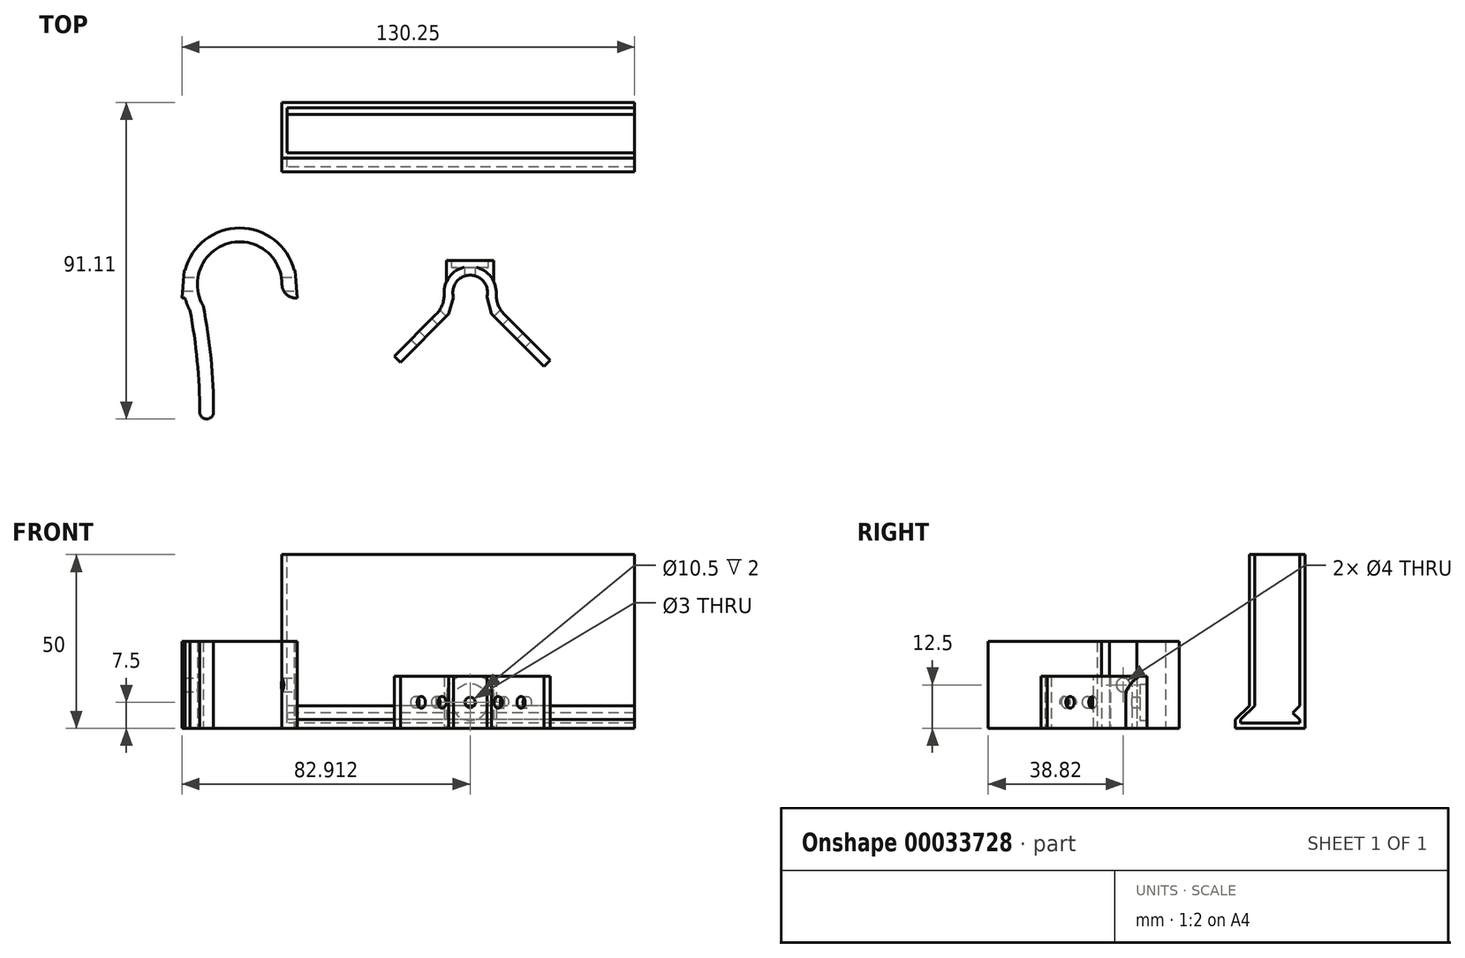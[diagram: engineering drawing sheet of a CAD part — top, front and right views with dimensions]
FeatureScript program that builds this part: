
annotation { "Feature Type Name" : "Feature", "Feature Type Description" : "" }
export const myFeature = defineFeature(function(context is Context, id is Id, definition is map)
    precondition{}
    {
        {
            var Q0;
            Q0=qCreatedBy(makeId("Top.planeOp"),FACE);
            var sketch = newSketch(context, id + "F0", { "sketchPlane" : qUnion([Q0])});
            skLineSegment(sketch, "E0", {"start": v(-6.16, 14.57) * mm, "end": v(-6.16, -16.07) * mm, "construction": true});
            skLineSegment(sketch, "E1.0", {"start": v(-21.16, 14.57) * mm, "end": v(-21.16, -16.07) * mm, "construction": true});
            skLineSegment(sketch, "E2.0", {"start": v(-24.16, 14.57) * mm, "end": v(-24.16, -16.07) * mm, "construction": true});
            skLineSegment(sketch, "E3.0", {"start": v(-3.16, 14.57) * mm, "end": v(-3.16, -16.07) * mm, "construction": true});
            skArc(sketch, "E4", {"start": v(-3.16, 14.57) * mm, "mid": v(-13.66, 32.92) * mm, "end": v(-24.16, 14.57) * mm});
            skArc(sketch, "E5", {"start": v(-21.16, -16.07) * mm, "mid": v(-21.91, -0.67) * mm, "end": v(-24.16, 14.57) * mm});
            skLineSegment(sketch, "E6", {"start": v(-13.66, 20.74) * mm, "end": v(-13.66, -32.7) * mm, "construction": true});
            skArc(sketch, "E7.0", {"start": v(-25.16, -16.07) * mm, "mid": v(-25.86, -1.38) * mm, "end": v(-27.97, 13.18) * mm});
            skArc(sketch, "E7.1", {"start": v(0.29, 12.55) * mm, "mid": v(-13.3, 36.92) * mm, "end": v(-27.97, 13.18) * mm});
            skArc(sketch, "E8", {"start": v(-25.16, -16.07) * mm, "mid": v(-23.16, -18.07) * mm, "end": v(-21.16, -16.07) * mm});
            skArc(sketch, "E9.MirrorCS", {"start": v(-6.16, -16.07) * mm, "mid": v(-5.4, -0.67) * mm, "end": v(-3.16, 14.57) * mm});
            skArc(sketch, "E10.MirrorCS", {"start": v(-2.16, -16.07) * mm, "mid": v(-1.46, -1.38) * mm, "end": v(0.64, 13.18) * mm});
            skArc(sketch, "E11.MirrorCS", {"start": v(-2.16, -16.07) * mm, "mid": v(-4.16, -18.07) * mm, "end": v(-6.16, -16.07) * mm});
            skCircle(sketch, "E12", {"center": v(-29.84, 20.74) * mm, "radius": 4 * mm});
            skLineSegment(sketch, "E13", {"start": v(-28.93, 31.84) * mm, "end": v(-30.86, 9.83) * mm});
            skLineSegment(sketch, "E14.MirrorCS", {"start": v(1.6, 31.84) * mm, "end": v(3.53, 9.83) * mm});
            skCircle(sketch, "E15.MirrorC", {"center": v(2.52, 20.74) * mm, "radius": 4 * mm});
            skSolve(sketch);
        }
        {
            var Q0;
            {var subQ6=sQuery(id+"F0.wireOp",EDGE,"E5");Q0=makeQuery(id+"F0.imprint","IMPRINT",FACE,{"disambiguationData":[TD([[makeQuery(id+"F0.imprint","IMPRINT",EDGE,{"derivedFrom":subQ6}),1.0]])]});}
            var Q1;
            {var subQ1=sQuery(id+"F0.wireOp",EDGE,"E9.MirrorCS");Q1=makeQuery(id+"F0.imprint","IMPRINT",FACE,{"disambiguationData":[TD([[makeQuery(id+"F0.imprint","IMPRINT",EDGE,{"derivedFrom":subQ1}),-1.0]])]});}
            var Q2;
            {var subQ0=sQuery(id+"F0.wireOp",EDGE,"E15.MirrorC");var subQ1=sQuery(id+"F0.wireOp",EDGE,"E4");var subQ2=makeQuery(id+"F0.imprint","INTERSECT",VERTEX,{"derivedFrom":[subQ1,subQ0]});Q2=makeQuery(id+"F0.imprint","IMPRINT",FACE,{"disambiguationData":[TD([[makeQuery(id+"F0.imprint","IMPRINT",EDGE,{"disambiguationData":[TD([[subQ2,-1.0]])],"derivedFrom":subQ1}),-1.0]])]});}
            var Q3;
            {var subQ0=sQuery(id+"F0.wireOp",EDGE,"E14.MirrorCS");var subQ1=sQuery(id+"F0.wireOp",EDGE,"E7.1");var subQ2=makeQuery(id+"F0.imprint","INTERSECT",VERTEX,{"derivedFrom":[subQ1,subQ0]});Q3=makeQuery(id+"F0.imprint","IMPRINT",FACE,{"disambiguationData":[TD([[makeQuery(id+"F0.imprint","IMPRINT",EDGE,{"disambiguationData":[TD([[subQ2,-1.0]])],"derivedFrom":subQ1}),-1.0]])]});}
            var Q4;
            {var subQ0=sQuery(id+"F0.wireOp",EDGE,"E13");var subQ1=sQuery(id+"F0.wireOp",EDGE,"E7.1");var subQ2=makeQuery(id+"F0.imprint","INTERSECT",VERTEX,{"derivedFrom":[subQ1,subQ0]});Q4=makeQuery(id+"F0.imprint","IMPRINT",FACE,{"disambiguationData":[TD([[makeQuery(id+"F0.imprint","IMPRINT",EDGE,{"disambiguationData":[TD([[subQ2,1.0]])],"derivedFrom":subQ1}),-1.0]])]});}
            var Q5;
            {var subQ0=sQuery(id+"F0.wireOp",EDGE,"E13");var subQ1=sQuery(id+"F0.wireOp",EDGE,"E7.1");var subQ2=makeQuery(id+"F0.imprint","INTERSECT",VERTEX,{"derivedFrom":[subQ1,subQ0]});Q5=makeQuery(id+"F0.imprint","IMPRINT",FACE,{"disambiguationData":[TD([[makeQuery(id+"F0.imprint","IMPRINT",EDGE,{"disambiguationData":[TD([[subQ2,-1.0]])],"derivedFrom":subQ1}),-1.0]])]});}
            var Q6;
            {var subQ0=sQuery(id+"F0.wireOp",EDGE,"E14.MirrorCS");var subQ1=sQuery(id+"F0.wireOp",EDGE,"E7.1");var subQ2=makeQuery(id+"F0.imprint","INTERSECT",VERTEX,{"derivedFrom":[subQ1,subQ0]});Q6=makeQuery(id+"F0.imprint","IMPRINT",FACE,{"disambiguationData":[TD([[makeQuery(id+"F0.imprint","IMPRINT",EDGE,{"disambiguationData":[TD([[subQ2,1.0]])],"derivedFrom":subQ1}),-1.0]])]});}
            var Q7;
            {var subQ0=sQuery(id+"F0.wireOp",EDGE,"E7.1");var subQ1=makeQuery(id+"F0.imprint","INTERSECT",VERTEX,{"derivedFrom":[subQ0,sQuery(id+"F0.wireOp",EDGE,"E14.MirrorCS")]});Q7=makeQuery(id+"F0.imprint","IMPRINT",FACE,{"disambiguationData":[TD([[makeQuery(id+"F0.imprint","IMPRINT",EDGE,{"disambiguationData":[TD([[subQ1,-1.0]])],"derivedFrom":subQ0}),1.0]])]});}
            var Q8;
            {var subQ0=sQuery(id+"F0.wireOp",EDGE,"E7.1");var subQ1=makeQuery(id+"F0.imprint","INTERSECT",VERTEX,{"derivedFrom":[subQ0,sQuery(id+"F0.wireOp",EDGE,"E13")]});Q8=makeQuery(id+"F0.imprint","IMPRINT",FACE,{"disambiguationData":[TD([[makeQuery(id+"F0.imprint","IMPRINT",EDGE,{"disambiguationData":[TD([[subQ1,1.0]])],"derivedFrom":subQ0}),1.0]])]});}
            extrude(context, id + "F1", {"entities" : qUnion([Q0, Q1, Q2, Q3, Q4, Q5, Q6, Q7, Q8]), "depth" : 25 * mm, "offsetDistance" : 25 * mm});
        }
        {
            var Q0;
            Q0=qCreatedBy(makeId("Right.planeOp"),FACE);
            var sketch = newSketch(context, id + "F2", { "sketchPlane" : qUnion([Q0])});
            skLineSegment(sketch, "E16.0.0", {"start": v(16.77, 0) * mm, "end": v(24.73, 0) * mm});
            skLineSegment(sketch, "E16.0.1", {"start": v(24.73, 0) * mm, "end": v(24.73, 25) * mm});
            skLineSegment(sketch, "E16.0.2", {"start": v(24.73, 25) * mm, "end": v(16.77, 25) * mm});
            skLineSegment(sketch, "E16.0.3", {"start": v(16.77, 25) * mm, "end": v(16.77, 0) * mm});
            skCircle(sketch, "E17", {"center": v(20.75, 12.5) * mm, "radius": 2 * mm});
            skPoint(sketch, "E17.centerSnap0", {"position": v(16.77, 12.5) * mm});
            skPoint(sketch, "E17.centerSnap1", {"position": v(20.75, 25) * mm});
            skSolve(sketch);
        }
        {
            var Q0;
            Q0=makeQuery(id+"F2.imprint","IMPRINT",FACE,{"disambiguationData":[TD([[makeQuery(id+"F2.imprint","IMPRINT",EDGE,{"derivedFrom":sQuery(id+"F2.wireOp",EDGE,"E17")}),1.0]])]});
            extrude(context, id + "F3", {"entities" : qUnion([Q0]), "operationType" : NewBodyOperationType.REMOVE, "oppositeDirection" : true, "depth" : 50 * mm, "offsetDistance" : 25 * mm, "hasSecondDirection" : true, "secondDirectionOppositeDirection" : false, "secondDirectionDepth" : 25 * mm});
        }
        {
            var Q0;
            Q0=qCreatedBy(makeId("Top.planeOp"),FACE);
            var sketch = newSketch(context, id + "F4", { "sketchPlane" : qUnion([Q0])});
            skLineSegment(sketch, "E18", {"start": v(32.57, -1.77) * mm, "end": v(49.13, 14.79) * mm});
            skLineSegment(sketch, "E19", {"start": v(56.2, 14.79) * mm, "end": v(73.87, -2.9) * mm});
            skArc(sketch, "E20", {"start": v(49.13, 14.79) * mm, "mid": v(52.66, 23.32) * mm, "end": v(56.2, 14.79) * mm});
            skLineSegment(sketch, "E21.0", {"start": v(59.43, 15.09) * mm, "end": v(75.64, -1.12) * mm});
            skArc(sketch, "E21.1", {"start": v(45.9, 15.09) * mm, "mid": v(52.66, 25.82) * mm, "end": v(59.43, 15.09) * mm});
            skLineSegment(sketch, "E21.2", {"start": v(30.8, 0) * mm, "end": v(45.9, 15.09) * mm});
            skLineSegment(sketch, "E22", {"start": v(30.8, 0) * mm, "end": v(32.57, -1.77) * mm});
            skLineSegment(sketch, "E23", {"start": v(73.87, -2.9) * mm, "end": v(75.64, -1.12) * mm});
            skLineSegment(sketch, "E24", {"start": v(45.9, 21.55) * mm, "end": v(45.9, 27.55) * mm});
            skLineSegment(sketch, "E25", {"start": v(52.66, 25.82) * mm, "end": v(36.68, 25.82) * mm});
            skLineSegment(sketch, "E26", {"start": v(45.9, 27.55) * mm, "end": v(59.43, 27.55) * mm});
            skLineSegment(sketch, "E27", {"start": v(59.43, 27.55) * mm, "end": v(59.43, 21.55) * mm});
            skSolve(sketch);
        }
        {
            var Q0;
            Q0 = qSketchRegion(id + "F4", true);
            extrude(context, id + "F5", {"entities" : qUnion([Q0]), "depth" : 15 * mm, "offsetDistance" : 25 * mm});
        }
        {
            var Q0;
            Q0=makeQuery(id+"F5.opExtrude","SWEPT_FACE",FACE,{"disambiguationData":[OSD([sQuery(id+"F4.wireOp",EDGE,"E26")])]});
            var sketch = newSketch(context, id + "F6", { "sketchPlane" : qUnion([Q0])});
            skCircle(sketch, "E28", {"center": v(-52.66, 7.5) * mm, "radius": 5.25 * mm});
            skPoint(sketch, "E28.centerSnap0", {"position": v(-45.9, 7.5) * mm});
            skPoint(sketch, "E28.centerSnap1", {"position": v(-52.66, 15) * mm});
            skCircle(sketch, "E29", {"center": v(-52.66, 7.5) * mm, "radius": 1.5 * mm});
            skSolve(sketch);
        }
        {
            var Q0;
            Q0 = qSketchRegion(id + "F6", true);
            extrude(context, id + "F7", {"entities" : qUnion([Q0]), "operationType" : NewBodyOperationType.REMOVE, "oppositeDirection" : true, "depth" : 2 * mm, "offsetDistance" : 25 * mm});
        }
        {
            var Q0;
            Q0=makeQuery(id+"F7.boolean.opBoolean","SPLIT",FACE,{"disambiguationData":[TD([makeQuery(id+"F7.opExtrude","SWEPT_FACE",FACE,{"disambiguationData":[OSD([sQuery(id+"F6.wireOp",EDGE,"E29")])]})])],"derivedFrom":makeQuery(id+"F5.opExtrude","SWEPT_FACE",FACE,{"disambiguationData":[OSD([sQuery(id+"F4.wireOp",EDGE,"E26")])]})});
            extrude(context, id + "F8", {"entities" : qUnion([Q0]), "operationType" : NewBodyOperationType.REMOVE, "endBound" : BoundingType.UP_TO_NEXT, "oppositeDirection" : true, "depth" : 25 * mm, "offsetDistance" : 25 * mm});
        }
        {
            var Q0;
            Q0=makeQuery(id+"F5.opExtrude","SWEPT_EDGE",EDGE,{"disambiguationData":[OSD([sQuery(id+"F4.wireOp",EDGE,"E21.0"),sQuery(id+"F4.wireOp",EDGE,"E21.1")])]});
            var Q1;
            Q1=makeQuery(id+"F5.opExtrude","SWEPT_EDGE",EDGE,{"disambiguationData":[OSD([sQuery(id+"F4.wireOp",EDGE,"E21.1"),sQuery(id+"F4.wireOp",EDGE,"E21.2")])]});
            fillet(context, id + "F9", {"entities" : qUnion([Q0, Q1]), "tangentPropagation" : true, "radius" : 8 * mm, "defaultsChanged" : true, "vertexSettings" : [], "allowEdgeOverflow" : false});
        }
        {
            var Q0;
            Q0=makeQuery(id+"F5.opExtrude","SWEPT_EDGE",EDGE,{"disambiguationData":[OSD([sQuery(id+"F4.wireOp",EDGE,"E19"),sQuery(id+"F4.wireOp",EDGE,"E20")])]});
            var Q1;
            Q1=makeQuery(id+"F5.opExtrude","SWEPT_EDGE",EDGE,{"disambiguationData":[OSD([sQuery(id+"F4.wireOp",EDGE,"E18"),sQuery(id+"F4.wireOp",EDGE,"E20")])]});
            chamfer(context, id + "F10", {"entities" : qUnion([Q0, Q1]), "width" : 5 * mm, "tangentPropagation" : true});
        }
        {
            var Q0;
            Q0=makeQuery(id+"F5.opExtrude","CAP_EDGE",EDGE,{"disambiguationData":[OSD([sQuery(id+"F4.wireOp",EDGE,"E24")])],"isStart":false});
            var Q1;
            Q1=makeQuery(id+"F5.opExtrude","CAP_EDGE",EDGE,{"disambiguationData":[OSD([sQuery(id+"F4.wireOp",EDGE,"E27")])],"isStart":false});
            fillet(context, id + "F11", {"entities" : qUnion([Q0, Q1]), "tangentPropagation" : true, "radius" : 5 * mm, "defaultsChanged" : false, "vertexSettings" : [], "allowEdgeOverflow" : false});
        }
        {
            var Q0;
            Q0=makeQuery(id+"F5.opExtrude","SWEPT_FACE",FACE,{"disambiguationData":[OSD([sQuery(id+"F4.wireOp",EDGE,"E21.0")])]});
            var sketch = newSketch(context, id + "F12", { "sketchPlane" : qUnion([Q0])});
            skPoint(sketch, "E30", {"position": v(-44.98, 7.5) * mm});
            skPoint(sketch, "E30.positionSnap0", {"position": v(-54.28, 7.5) * mm});
            skPoint(sketch, "E30.positionSnap1", {"position": v(-44.98, 15) * mm});
            skPoint(sketch, "E31", {"position": v(-35.68, 7.5) * mm});
            skSolve(sketch);
        }
        {
            var Q0;
            Q0=makeQuery(id+"F5.opExtrude","SWEPT_FACE",FACE,{"disambiguationData":[OSD([sQuery(id+"F4.wireOp",EDGE,"E21.2")])]});
            var sketch = newSketch(context, id + "F13", { "sketchPlane" : qUnion([Q0])});
            skPoint(sketch, "E32", {"position": v(-30.29, 7.5) * mm});
            skPoint(sketch, "E32.positionSnap0", {"position": v(-30.29, 0) * mm});
            skPoint(sketch, "E32.positionSnap1", {"position": v(-21.78, 7.5) * mm});
            skPoint(sketch, "E33", {"position": v(-38.8, 7.5) * mm});
            skSolve(sketch);
        }
        {
            var Q0;
            Q0=sQuery(id+"F13.wireOp",VERTEX,"E33");
            var Q1;
            Q1=sQuery(id+"F13.wireOp",VERTEX,"E32");
            var Q2;
            Q2=sQuery(id+"F12.wireOp",VERTEX,"E31");
            var Q3;
            Q3=sQuery(id+"F12.wireOp",VERTEX,"E30");
            var Q4;
            Q4=makeQuery(id+"F5.opExtrude","SWEPT_BODY",BODY,{"disambiguationData":[OSD([sQuery(id+"F4.wireOp",EDGE,"E18"),sQuery(id+"F4.wireOp",EDGE,"E19"),sQuery(id+"F4.wireOp",EDGE,"E20"),sQuery(id+"F4.wireOp",EDGE,"E21.0"),sQuery(id+"F4.wireOp",EDGE,"E21.1"),sQuery(id+"F4.wireOp",EDGE,"E21.2"),sQuery(id+"F4.wireOp",EDGE,"E22"),sQuery(id+"F4.wireOp",EDGE,"E23"),sQuery(id+"F4.wireOp",EDGE,"E24"),sQuery(id+"F4.wireOp",EDGE,"E26"),sQuery(id+"F4.wireOp",EDGE,"E27")])]});
            hole(context, id + "F14", {"style" : HoleStyle.SIMPLE, "endStyle" : HoleEndStyle.THROUGH, "holeDiameter" : 3.4 * mm, "majorDiameter" : 5 * mm, "isTappedThrough" : true, "tappedDepth" : 12 * mm, "tapClearance" : 3, "locations" : qUnion([Q0, Q1, Q2, Q3]), "scope" : qUnion([Q4])});
        }
        {
            var Q0;
            Q0=qCreatedBy(makeId("Right.planeOp"),FACE);
            var sketch = newSketch(context, id + "F15", { "sketchPlane" : qUnion([Q0])});
            skLineSegment(sketch, "E34.bottom", {"start": v(53.04, 0) * mm, "end": v(73.04, 0) * mm});
            skLineSegment(sketch, "E34.top", {"start": v(53.04, 50) * mm, "end": v(73.04, 50) * mm});
            skLineSegment(sketch, "E34.left", {"start": v(53.04, 0) * mm, "end": v(53.04, 2.5) * mm});
            skLineSegment(sketch, "E34.right", {"start": v(73.04, 0) * mm, "end": v(73.04, 50) * mm});
            skLineSegment(sketch, "E35.0", {"start": v(71.54, 1.5) * mm, "end": v(71.54, 50) * mm});
            skLineSegment(sketch, "E35.1", {"start": v(54.54, 1.5) * mm, "end": v(71.54, 1.5) * mm});
            skLineSegment(sketch, "E35.2", {"start": v(54.54, 1.5) * mm, "end": v(54.54, 2.5) * mm});
            skLineSegment(sketch, "E36", {"start": v(71.54, 4.5) * mm, "end": v(69.54, 4.5) * mm});
            skLineSegment(sketch, "E37", {"start": v(69.54, 4.5) * mm, "end": v(71.54, 2.5) * mm});
            skLineSegment(sketch, "E38", {"start": v(69.54, 4.5) * mm, "end": v(71.54, 6.5) * mm});
            skLineSegment(sketch, "E39", {"start": v(63.04, 0) * mm, "end": v(63.04, 7.78) * mm, "construction": true});
            skLineSegment(sketch, "E40.MirrorCS", {"start": v(56.54, 4.5) * mm, "end": v(54.54, 2.5) * mm});
            skLineSegment(sketch, "E41", {"start": v(56.54, 4.5) * mm, "end": v(58.54, 6.5) * mm});
            skLineSegment(sketch, "E42", {"start": v(58.54, 6.5) * mm, "end": v(58.54, 50) * mm});
            skLineSegment(sketch, "E43.0", {"start": v(57.04, 6.5) * mm, "end": v(57.04, 50) * mm});
            skLineSegment(sketch, "E44", {"start": v(57.04, 6.5) * mm, "end": v(53.04, 2.5) * mm});
            skSolve(sketch);
        }
        {
            var Q0;
            Q0=makeQuery(id+"F15.imprint","IMPRINT",FACE,{"disambiguationData":[TD([[makeQuery(id+"F15.imprint","IMPRINT",EDGE,{"derivedFrom":sQuery(id+"F15.wireOp",EDGE,"E34.bottom")}),1.0]])]});
            var Q1;
            {var subQ2=sQuery(id+"F15.wireOp",EDGE,"E36");Q1=makeQuery(id+"F15.imprint","IMPRINT",FACE,{"disambiguationData":[TD([[makeQuery(id+"F15.imprint","IMPRINT",EDGE,{"derivedFrom":subQ2}),-1.0]])]});}
            var Q2;
            {var subQ2=sQuery(id+"F15.wireOp",EDGE,"E36");Q2=makeQuery(id+"F15.imprint","IMPRINT",FACE,{"disambiguationData":[TD([[makeQuery(id+"F15.imprint","IMPRINT",EDGE,{"derivedFrom":subQ2}),1.0]])]});}
            var Q3;
            {var subQ0=sQuery(id+"F15.wireOp",EDGE,"E35.1");Q3=makeQuery(id+"F15.imprint","IMPRINT",FACE,{"disambiguationData":[TD([[makeQuery(id+"F15.imprint","IMPRINT",EDGE,{"derivedFrom":subQ0}),1.0]])]});}
            extrude(context, id + "F16", {"entities" : qUnion([Q0, Q1, Q2, Q3]), "depth" : 100 * mm, "offsetDistance" : 25 * mm, "hasSecondDirection" : true, "secondDirectionOppositeDirection" : true, "secondDirectionDepth" : 1.5 * mm});
        }
        {
            var Q0;
            {var subQ0=sQuery(id+"F15.wireOp",EDGE,"E35.1");Q0=makeQuery(id+"F15.imprint","IMPRINT",FACE,{"disambiguationData":[TD([[makeQuery(id+"F15.imprint","IMPRINT",EDGE,{"derivedFrom":subQ0}),1.0]])]});}
            extrude(context, id + "F17", {"entities" : qUnion([Q0]), "operationType" : NewBodyOperationType.REMOVE, "depth" : 100 * mm, "offsetDistance" : 25 * mm});
        }
    });
